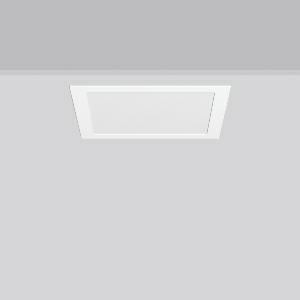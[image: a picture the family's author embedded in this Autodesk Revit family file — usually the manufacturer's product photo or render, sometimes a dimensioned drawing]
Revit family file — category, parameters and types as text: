
# Revit family: toledo_flat_square_e_672244_002_1_89_b2a8
name_source: partatom
category: Lighting Fixtures
units: mm (PartAtom-declared; Revit-internal decimal feet)

## family parameters
Cut with Voids When Loaded = No
Host = Face
Light Source = No
Part Type = Normal
Room Calculation Point = No
Round Connector Dimension = Use Diameter
Shared = No

## types (1)
- TOLEDO FLAT square E (1 x LED Modul 840, 2200 lm, 4000)
    Apparent Load = 23 VA
    CIE Flux Codes = 49 80 96 100 100
    Color Rendering = 80
    Color Temperature = 4000
    Default Elevation = 1800 mm
    Description = Series: TOLEDO FLAT square
Square recessed downlight. For escape route illumination. Housing: die-cast aluminium, powder-coated. Lightguide and diffuser made of non-yellowing plastic (PMMA). Diffuser opal matt plastic. Ceiling installation with spring system. Including separate LED converter with connecting cable 250 mm. Suitable for connection to central battery systems. With AC Control monitoring module for LUXIFAIR central battery units. External driver with simple plug-in locking system. 
Colour: white
Length: 300 mm
Width: 300 mm
Height: 3 mm
Cut-out length: 280 mm
Cut-out width: 280 mm
Recess height: 40 mm
Luminaire: recess height: 37-57 mm
Weight: 1.97 kg
Operating mode: maintained power mode
Lamp: LED
Socket: without socket
Colour temperature: 4000K
Colour rendering index (CRI): 80
System power: 23 W
Rated luminous flux: 2200 lm
Luminous flux, emergency: 2200 lm
System power, emergency: 23 W
Control gear: Regulated power supply
Protection class: I
Type of protection: IP 54
    Height = 0 mm  [stored 0 ft]
    Lamp = 1 x LED Modul 840
    Lamp Light Flux = 2200 lm
    Lamp count = 1
    Length = 300 mm
    Lifetime = 50000 h
    Luminous efficacy = 96 lm/W
    Manufacturer = RZB
    ModVariant = No
    Model = 672244.002.1.89
    Mounting Place = Ceiling
    Mounting Type = Recessed
    Number of Poles = 1
    OnlyDefault = Yes
    Power Factor = 1
    Product Name = TOLEDO FLAT square E
    Product group = Recessed downlights
    ProductGroupID = 402
    Protection Class = Protection class I
    Protection Degree = IP 40
    RLX_Detail_Level = 1
    RLX_Emergency_Light_Flux = 2200 lm
    RLX_Emergency_Type = 3
    RLX_Emergency_Type_DB = Yes
    RlxData = <blob elided: 12913 chars, md5=586f54e3>
    Socket = socket
    Standby Power = 0 W
    System Light Flux = 2200 lm
    System Power = 23 W
    Type Comments = Product without accessories
    Type Image = 901488.002.jpg
    URL = http://relux.com
    VarID = ---
    Voltage = 230 V
    Voltage Range = 220-240 V
    Weight = 0.00 kg
    Width = 300 mm

note: [stored X ft] marks values corroborated as IEEE doubles in the binary element streams (Revit-internal decimal feet)

## geometry (parser evidence)
native form markers: Sweep x11
no freeform markers — native parametric forms only
